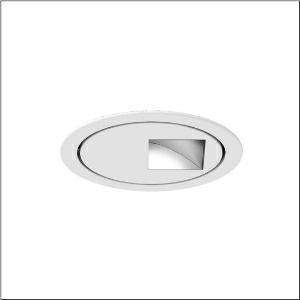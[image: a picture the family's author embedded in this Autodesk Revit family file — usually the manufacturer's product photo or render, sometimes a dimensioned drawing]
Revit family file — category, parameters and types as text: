
# Revit family: lunis_11_mini_round_51dk11b72wn21
name_source: partatom
category: Lighting Fixtures
units: mm (PartAtom-declared; Revit-internal decimal feet)

## family parameters
Cut with Voids When Loaded = No
Host = Face
Light Source = No
Part Type = Normal
Room Calculation Point = No
Round Connector Dimension = Use Diameter
Shared = No

## types (1)
- Lunis 11 mini round (1 x LED 4000K / CRI = 90 (unbekannt), 2120 lm, 4000K)
    Apparent Load = 28 VA
    CIE Flux Codes = 44 77 97 100 100
    Color Rendering = 90
    Color Temperature = 4000K
    Default Elevation = 1800 mm
    Description = Lunis 11 mini round, downlight, light control with wallwasher, of highly reflective aluminium, highly specular, light emission: direct distribution, LED rated luminous flux: 2.120lm, light colour: 940, control gear: ECG, with terminal, 3-pole, mains connection: 220..230V, AC/DC, 0/50..60Hz, LED module, luminaire module, of aluminium, highly specular, white, diameter: 176mm, clamping range: 1..40mm, recessing ring, of plastic, traffic white (RAL 9016), protection rating (complete): IP20, insulation class (complete): insulation class II (safety insulation), certification: CE, permissible ambient temperature for indoor applications: 0..+35°C, packaging unit: 1 piece
    Height = 0 mm  [stored 0 ft]
    Lamp = 1 x LED 4000K / CRI >= 90 (unbekannt)
    Lamp Light Flux = 2120 lm
    Lamp count = 1
    Length = 176 mm
    Luminous efficacy = 75 lm/W
    Manufacturer = Siteco
    ModVariant = No
    Model = 51DK11B72WN21
    Mounting Place = Ceiling
    Mounting Type = Recessed
    Number of Poles = 1
    OnlyDefault = Yes
    Power Factor = 1
    Product Name = Lunis 11 mini round
    Product group = downlight
    ProductGroupID = 400
    Protection Class = Protection class II
    Protection Degree = IP 20
    RLX_Detail_Level = 1
    RLX_Emergency_Light_Flux = 0 lm
    RLX_Emergency_Type = 0
    RLX_Emergency_Type_DB = No
    RlxData = <blob elided: 59345 chars, md5=234be712>
    Socket = socket
    Standby Power = 0 W
    System Light Flux = 2120 lm
    System Power = 28 W
    Type Comments = Product without accessories
    Type Image = l_1004772.jpg
    URL = http://relux.com
    VarID = ---
    Voltage = 0 V
    Weight = 0.00 kg
    Width = 176 mm

note: [stored X ft] marks values corroborated as IEEE doubles in the binary element streams (Revit-internal decimal feet)

## geometry (parser evidence)
native form markers: Blend x4, Sweep x10
no freeform markers — native parametric forms only
